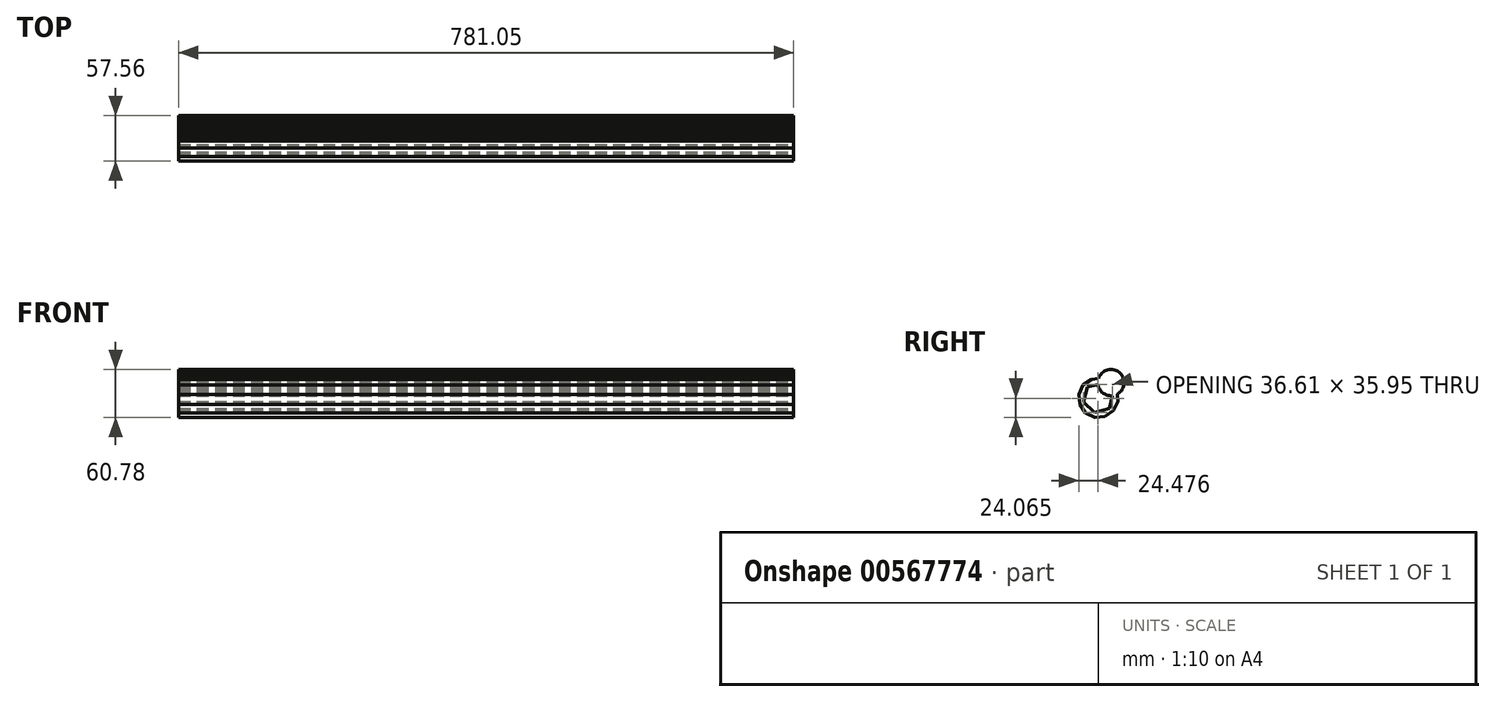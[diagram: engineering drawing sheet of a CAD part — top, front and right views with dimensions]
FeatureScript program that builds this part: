
annotation { "Feature Type Name" : "Feature", "Feature Type Description" : "" }
export const myFeature = defineFeature(function(context is Context, id is Id, definition is map)
    precondition{}
    {
        {
            var Q0;
            Q0=qCreatedBy(makeId("Right.planeOp"),FACE);
            var sketch = newSketch(context, id + "F0", { "sketchPlane" : qUnion([Q0])});
            skCircle(sketch, "E0.cCircle", {"center": v(-33.6, 27.27) * mm, "radius": 24.3 * mm, "construction": true});
            skLineSegment(sketch, "E0.0", {"start": v(-49.73, 7.95) * mm, "end": v(-57.22, 18.6) * mm});
            skLineSegment(sketch, "E0.1", {"start": v(-57.22, 18.6) * mm, "end": v(-58.4, 31.57) * mm});
            skLineSegment(sketch, "E0.2", {"start": v(-58.4, 31.57) * mm, "end": v(-52.92, 43.4) * mm});
            skLineSegment(sketch, "E0.3", {"start": v(-52.92, 43.4) * mm, "end": v(-42.27, 50.89) * mm});
            skLineSegment(sketch, "E0.4", {"start": v(-42.27, 50.89) * mm, "end": v(-29.3, 52.06) * mm});
            skLineSegment(sketch, "E0.5", {"start": v(-29.3, 52.06) * mm, "end": v(-17.48, 46.59) * mm});
            skLineSegment(sketch, "E0.6", {"start": v(-17.48, 46.59) * mm, "end": v(-9.98, 35.94) * mm});
            skLineSegment(sketch, "E0.7", {"start": v(-9.98, 35.94) * mm, "end": v(-8.82, 22.97) * mm});
            skLineSegment(sketch, "E0.8", {"start": v(-8.82, 22.97) * mm, "end": v(-14.29, 11.15) * mm});
            skLineSegment(sketch, "E0.9", {"start": v(-14.29, 11.15) * mm, "end": v(-24.94, 3.65) * mm});
            skLineSegment(sketch, "E0.10", {"start": v(-24.94, 3.65) * mm, "end": v(-37.9, 2.48) * mm});
            skLineSegment(sketch, "E0.11", {"start": v(-37.9, 2.48) * mm, "end": v(-49.73, 7.95) * mm});
            skPoint(sketch, "E0.0.midPoint", {"position": v(-53.48, 13.28) * mm});
            skCircle(sketch, "E1.cCircle", {"center": v(-33.6, 27.27) * mm, "radius": 16.73 * mm, "construction": true});
            skLineSegment(sketch, "E1.0", {"start": v(-19.84, 13.72) * mm, "end": v(-38.45, 8.57) * mm});
            skLineSegment(sketch, "E1.1", {"start": v(-38.45, 8.57) * mm, "end": v(-52.22, 22.12) * mm});
            skLineSegment(sketch, "E1.2", {"start": v(-52.22, 22.12) * mm, "end": v(-47.37, 40.82) * mm});
            skLineSegment(sketch, "E1.3", {"start": v(-47.37, 40.82) * mm, "end": v(-28.76, 45.97) * mm});
            skLineSegment(sketch, "E1.4", {"start": v(-28.76, 45.97) * mm, "end": v(-14.99, 32.42) * mm});
            skLineSegment(sketch, "E1.5", {"start": v(-14.99, 32.42) * mm, "end": v(-19.84, 13.72) * mm});
            skPoint(sketch, "E1.0.midPoint", {"position": v(-29.14, 11.15) * mm});
            skCircle(sketch, "E2.cCircle", {"center": v(-17.48, 46.59) * mm, "radius": 16.64 * mm, "construction": true});
            skLineSegment(sketch, "E2.0", {"start": v(-23.53, 31.04) * mm, "end": v(-25.43, 31.92) * mm});
            skLineSegment(sketch, "E2.1", {"start": v(-25.43, 31.92) * mm, "end": v(-27.2, 33.03) * mm});
            skLineSegment(sketch, "E2.2", {"start": v(-27.2, 33.03) * mm, "end": v(-28.82, 34.36) * mm});
            skLineSegment(sketch, "E2.3", {"start": v(-28.82, 34.36) * mm, "end": v(-30.27, 35.88) * mm});
            skLineSegment(sketch, "E2.4", {"start": v(-30.27, 35.88) * mm, "end": v(-31.5, 37.56) * mm});
            skLineSegment(sketch, "E2.5", {"start": v(-31.5, 37.56) * mm, "end": v(-32.53, 39.4) * mm});
            skLineSegment(sketch, "E2.6", {"start": v(-32.53, 39.4) * mm, "end": v(-33.31, 41.34) * mm});
            skLineSegment(sketch, "E2.7", {"start": v(-33.31, 41.34) * mm, "end": v(-33.85, 43.36) * mm});
            skLineSegment(sketch, "E2.8", {"start": v(-33.85, 43.36) * mm, "end": v(-34.12, 45.44) * mm});
            skLineSegment(sketch, "E2.9", {"start": v(-34.12, 45.44) * mm, "end": v(-34.13, 47.53) * mm});
            skLineSegment(sketch, "E2.10", {"start": v(-34.13, 47.53) * mm, "end": v(-33.88, 49.61) * mm});
            skLineSegment(sketch, "E2.11", {"start": v(-33.88, 49.61) * mm, "end": v(-33.37, 51.64) * mm});
            skLineSegment(sketch, "E2.12", {"start": v(-33.37, 51.64) * mm, "end": v(-32.62, 53.6) * mm});
            skLineSegment(sketch, "E2.13", {"start": v(-32.62, 53.6) * mm, "end": v(-31.62, 55.44) * mm});
            skLineSegment(sketch, "E2.14", {"start": v(-31.62, 55.44) * mm, "end": v(-30.4, 57.14) * mm});
            skLineSegment(sketch, "E2.15", {"start": v(-30.4, 57.14) * mm, "end": v(-28.97, 58.67) * mm});
            skLineSegment(sketch, "E2.16", {"start": v(-28.97, 58.67) * mm, "end": v(-27.37, 60.02) * mm});
            skLineSegment(sketch, "E2.17", {"start": v(-27.37, 60.02) * mm, "end": v(-25.6, 61.15) * mm});
            skLineSegment(sketch, "E2.18", {"start": v(-25.6, 61.15) * mm, "end": v(-23.72, 62.05) * mm});
            skLineSegment(sketch, "E2.19", {"start": v(-23.72, 62.05) * mm, "end": v(-21.73, 62.71) * mm});
            skLineSegment(sketch, "E2.20", {"start": v(-21.73, 62.71) * mm, "end": v(-19.67, 63.12) * mm});
            skLineSegment(sketch, "E2.21", {"start": v(-19.67, 63.12) * mm, "end": v(-17.58, 63.26) * mm});
            skLineSegment(sketch, "E2.22", {"start": v(-17.58, 63.26) * mm, "end": v(-15.5, 63.14) * mm});
            skLineSegment(sketch, "E2.23", {"start": v(-15.5, 63.14) * mm, "end": v(-13.43, 62.76) * mm});
            skLineSegment(sketch, "E2.24", {"start": v(-13.43, 62.76) * mm, "end": v(-11.44, 62.13) * mm});
            skLineSegment(sketch, "E2.25", {"start": v(-11.44, 62.13) * mm, "end": v(-9.54, 61.25) * mm});
            skLineSegment(sketch, "E2.26", {"start": v(-9.54, 61.25) * mm, "end": v(-7.76, 60.14) * mm});
            skLineSegment(sketch, "E2.27", {"start": v(-7.76, 60.14) * mm, "end": v(-6.14, 58.81) * mm});
            skLineSegment(sketch, "E2.28", {"start": v(-6.14, 58.81) * mm, "end": v(-4.7, 57.3) * mm});
            skLineSegment(sketch, "E2.29", {"start": v(-4.7, 57.3) * mm, "end": v(-3.46, 55.6) * mm});
            skLineSegment(sketch, "E2.30", {"start": v(-3.46, 55.6) * mm, "end": v(-2.44, 53.78) * mm});
            skLineSegment(sketch, "E2.31", {"start": v(-2.44, 53.78) * mm, "end": v(-1.65, 51.84) * mm});
            skLineSegment(sketch, "E2.32", {"start": v(-1.65, 51.84) * mm, "end": v(-1.12, 49.8) * mm});
            skLineSegment(sketch, "E2.33", {"start": v(-1.12, 49.8) * mm, "end": v(-0.84, 47.73) * mm});
            skLineSegment(sketch, "E2.34", {"start": v(-0.84, 47.73) * mm, "end": v(-0.83, 45.64) * mm});
            skLineSegment(sketch, "E2.35", {"start": v(-0.83, 45.64) * mm, "end": v(-1.08, 43.56) * mm});
            skLineSegment(sketch, "E2.36", {"start": v(-1.08, 43.56) * mm, "end": v(-1.6, 41.53) * mm});
            skLineSegment(sketch, "E2.37", {"start": v(-1.6, 41.53) * mm, "end": v(-2.35, 39.58) * mm});
            skLineSegment(sketch, "E2.38", {"start": v(-2.35, 39.58) * mm, "end": v(-3.35, 37.73) * mm});
            skLineSegment(sketch, "E2.39", {"start": v(-3.35, 37.73) * mm, "end": v(-4.57, 36.03) * mm});
            skLineSegment(sketch, "E2.40", {"start": v(-4.57, 36.03) * mm, "end": v(-6, 34.5) * mm});
            skLineSegment(sketch, "E2.41", {"start": v(-6, 34.5) * mm, "end": v(-7.6, 33.15) * mm});
            skLineSegment(sketch, "E2.42", {"start": v(-7.6, 33.15) * mm, "end": v(-9.36, 32.02) * mm});
            skLineSegment(sketch, "E2.43", {"start": v(-9.36, 32.02) * mm, "end": v(-11.25, 31.12) * mm});
            skLineSegment(sketch, "E2.44", {"start": v(-11.25, 31.12) * mm, "end": v(-13.24, 30.46) * mm});
            skLineSegment(sketch, "E2.45", {"start": v(-13.24, 30.46) * mm, "end": v(-15.3, 30.05) * mm});
            skLineSegment(sketch, "E2.46", {"start": v(-15.3, 30.05) * mm, "end": v(-17.38, 29.9) * mm});
            skLineSegment(sketch, "E2.47", {"start": v(-17.38, 29.9) * mm, "end": v(-19.47, 30.03) * mm});
            skLineSegment(sketch, "E2.48", {"start": v(-19.47, 30.03) * mm, "end": v(-21.53, 30.4) * mm});
            skLineSegment(sketch, "E2.49", {"start": v(-21.53, 30.4) * mm, "end": v(-23.53, 31.04) * mm});
            skPoint(sketch, "E2.0.midPoint", {"position": v(-24.48, 31.48) * mm});
            skSolve(sketch);
        }
        {
            var Q0;
            Q0=makeQuery(id+"F0.imprint","IMPRINT",FACE,{"disambiguationData":[TD([[makeQuery(id+"F0.imprint","IMPRINT",EDGE,{"derivedFrom":sQuery(id+"F0.wireOp",EDGE,"E0.0")}),-1.0]])]});
            var Q1;
            {var subQ4=sQuery(id+"F0.wireOp",EDGE,"E1.4");Q1=makeQuery(id+"F0.imprint","IMPRINT",FACE,{"disambiguationData":[TD([[makeQuery(id+"F0.imprint","IMPRINT",EDGE,{"derivedFrom":subQ4}),-1.0]])]});}
            var Q2;
            {var subQ4=sQuery(id+"F0.wireOp",EDGE,"E0.5");Q2=makeQuery(id+"F0.imprint","IMPRINT",FACE,{"disambiguationData":[TD([[makeQuery(id+"F0.imprint","IMPRINT",EDGE,{"derivedFrom":subQ4}),1.0]])]});}
            var Q3;
            {var subQ12=sQuery(id+"F0.wireOp",EDGE,"E0.5");Q3=makeQuery(id+"F0.imprint","IMPRINT",FACE,{"disambiguationData":[TD([[makeQuery(id+"F0.imprint","IMPRINT",EDGE,{"derivedFrom":subQ12}),-1.0]])]});}
            extrude(context, id + "F1", {"entities" : qUnion([Q0, Q1, Q2, Q3]), "oppositeDirection" : true, "depth" : 781.05 * mm, "offsetDistance" : 25.4 * mm});
        }
    });
